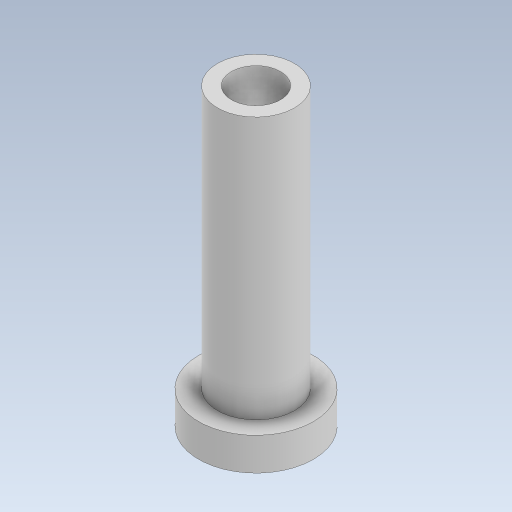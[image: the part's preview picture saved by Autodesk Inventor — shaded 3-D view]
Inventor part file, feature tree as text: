
AUTODESK INVENTOR PART (.ipt)
format: ipt  version: 2023.5 (Build 275446000, 446)  size: 265,728 bytes
history: native  units: mm
features: extrude x2, sketch x1
ambient origin geometry x8: Origin, YZ Plane, XZ Plane, XY Plane, X Axis, Y Axis, Z Axis, Center Point
bodies: Solid1 (feature_tree)
feature tree (3):
  sketch  "Sketch1"  dims[d0=4.7mm d1=7.0mm d2=3.0mm d3=2.0mm d4=0.0mm d5=18.0mm d6=0.0mm]
  extrude  "Extrusion1"  Depth=18.0mm
  extrude  "Extrusion2"  Depth=18.0mm
